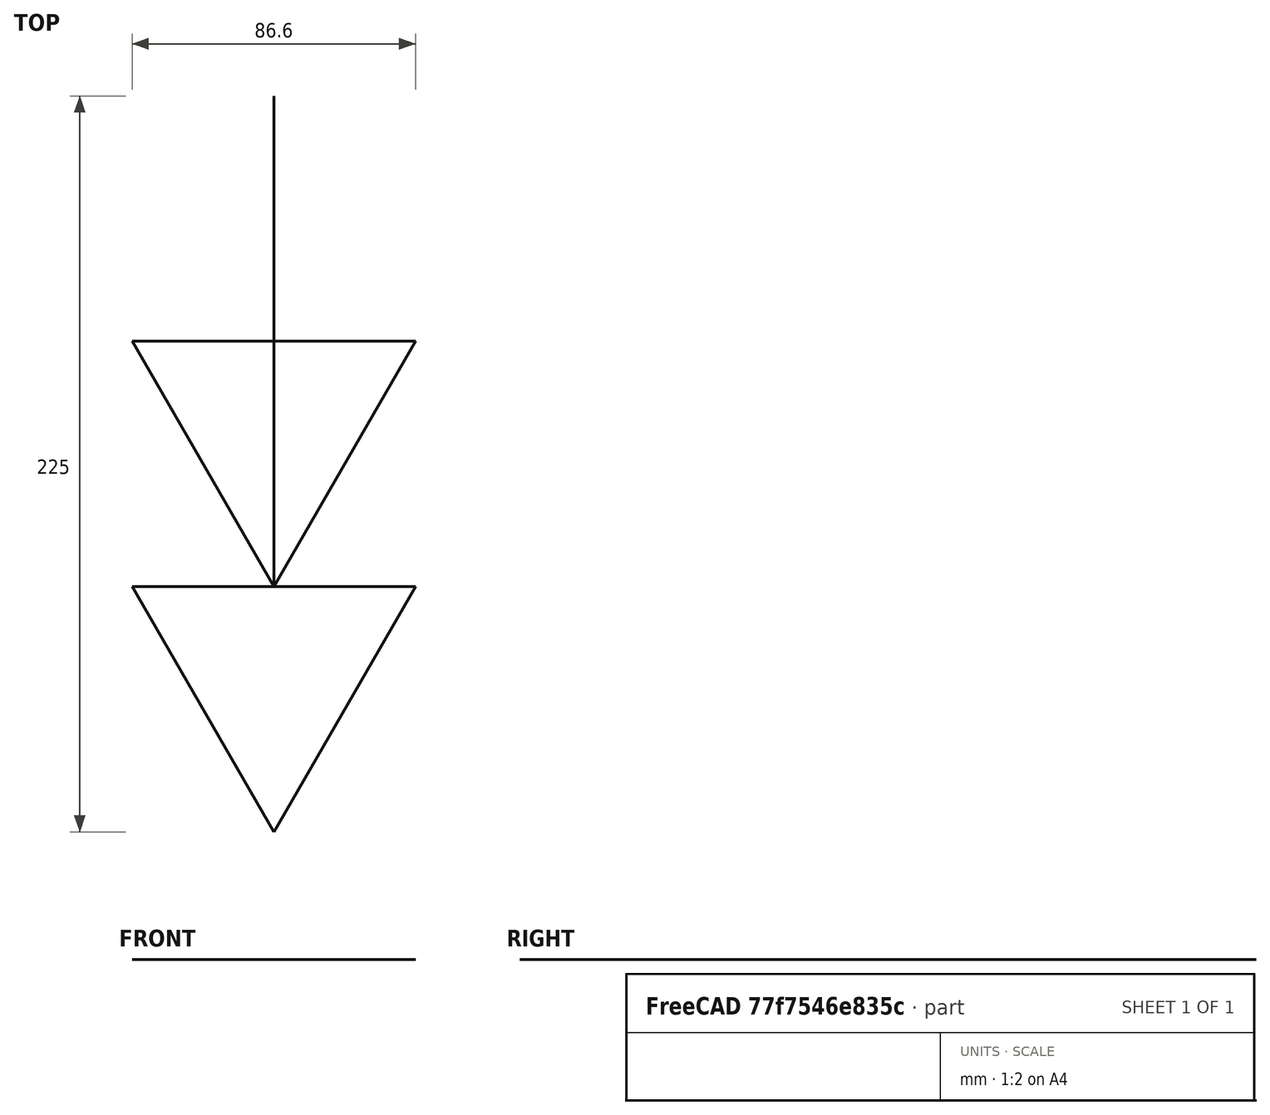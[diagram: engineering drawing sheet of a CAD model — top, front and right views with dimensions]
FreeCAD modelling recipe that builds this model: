
FCSTD DOCUMENT  (FreeCAD 1.1R20260325 (Git shallow))
Label: Tomada_Alta_2modulo_220v_com_simbologia
License: All rights reserved
LicenseURL: http://en.wikipedia.org/wiki/All_rights_reserved
objects: Part::FeaturePython×1, Part::Feature×1, App::DocumentObjectGroup×1
note: 2 computed .brp shape members not serialized (recipe doc carries the construction recipe); baked Part::Feature solids carry a one-line shape summary decoded from their .brp

FEATURE [Part::FeaturePython] Component  label="Tomada_2modulos_110v_alta"  # Arch/BIM 0 (typed FeaturePython)
  HorizontalArea = 0
  IfcData = attributes={"GlobalId": {"name": "GlobalId", "type": "IfcGloballyUniqueId", "is_enum": false, "enum_values": []}, "Description": {"... (+538 chars omitted),+1 more (map truncated)
  IfcType = 0
  MoveBase = false
  MoveWithHost = false
  PerimeterLength = 0
  Placement = pos=(0,0,2250) rot=(0,0,1;0rad)
  PredefinedType = 0
  VerticalArea = 0
FEATURE [Part::Feature] Compound002002002004005002002003003002003005002002005002002002002002002003  label="Simbologia_Tomada_alta"
  Placement = pos=(-87.5918,335.685,2241.87) rot=(0,0,1;0rad)
  shape: bbox 86.6 x 225 x 2e-07 mm, 2 faces, 0 solids (baked)
FEATURE [App::DocumentObjectGroup] Group  label="Tomada_2modulos_Alta"
  Group = -> [Component,Compound002002002004005002002003003002003005002002005002002002002002002003]
